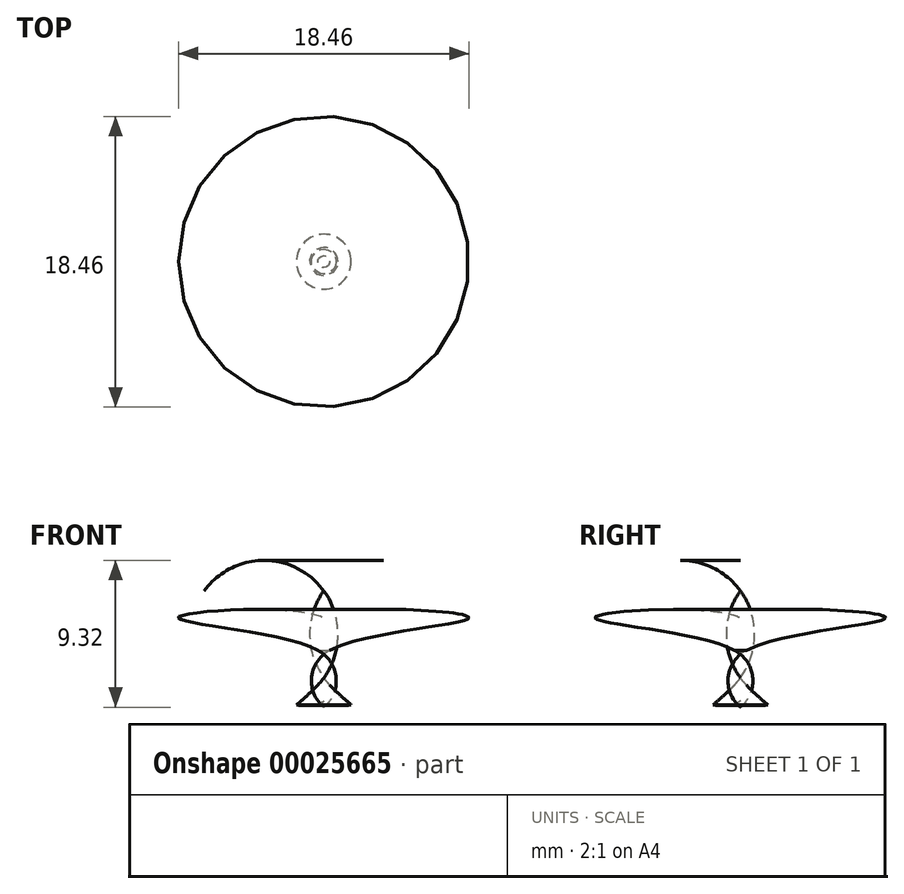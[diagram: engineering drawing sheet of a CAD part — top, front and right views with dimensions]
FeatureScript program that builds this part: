
annotation { "Feature Type Name" : "Feature", "Feature Type Description" : "" }
export const myFeature = defineFeature(function(context is Context, id is Id, definition is map)
    precondition{}
    {
        {
            var Q0;
            Q0=qCreatedBy(makeId("Front.planeOp"),FACE);
            var sketch = newSketch(context, id + "F0", { "sketchPlane" : qUnion([Q0])});
            skPoint(sketch, "E0.end.orphan", {"position": v(-15.16, 0) * mm});
            skPoint(sketch, "E1.end.orphan", {"position": v(0, 14.3) * mm});
            skPoint(sketch, "E1.start.orphan", {"position": v(0, 0) * mm});
            skPoint(sketch, "E2.endDerivative.orphan", {"position": v(-9.23, -2.95) * mm});
            skPoint(sketch, "E2.start.orphan", {"position": v(5.64, 0) * mm});
            skPoint(sketch, "E2.startDerivative.orphan", {"position": v(-9.23, 5.55) * mm});
            skFitSpline(sketch, "E3", {"points": [v(-1.74, 0) * mm, v(0, 3.22) * mm, v(-9.23, 5.55) * mm, v(0, 5.55) * mm, v(0, 4) * mm], "startDerivative": vector(19.84, 17.26) * mm, "endDerivative": vector(-7.42, -13.19) * mm});
            skLineSegment(sketch, "E4", {"start": v(0, 0) * mm, "end": v(0, 19.23) * mm});
            skFitSpline(sketch, "E5.trimOffspring", {"points": [v(-1.74, 0) * mm, v(0, 3.22) * mm, v(-9.23, 5.55) * mm, v(0, 5.55) * mm, v(0, 4) * mm], "startDerivative": vector(19.84, 17.26) * mm, "endDerivative": vector(-7.42, -13.19) * mm});
            skFitSpline(sketch, "E6", {"points": [v(-0.38, 1.19) * mm, v(-0.38, 3.48) * mm], "startDerivative": vector(0, 2.29) * mm, "endDerivative": vector(0, 2.29) * mm});
            skFitSpline(sketch, "E7", {"points": [v(-1.74, 0) * mm, v(-0.55, 0) * mm, v(0, 0.25) * mm], "startDerivative": vector(2.25, -0.18) * mm, "endDerivative": vector(1.18, 0.73) * mm});
            skSolve(sketch);
        }
        {
            var Q0;
            {var subQ3=sQuery(id+"F0.wireOp",EDGE,"E3");Q0=makeQuery(id+"F0.imprint","IMPRINT",FACE,{"disambiguationData":[TD([[makeQuery(id+"F0.imprint","IMPRINT",EDGE,{"derivedFrom":subQ3}),-1.0]])]});}
            var Q1;
            Q1=sQuery(id+"F0.wireOp",EDGE,"E4");
            revolve(context, id + "F1", {"entities" : qUnion([Q0]), "axis" : qUnion([Q1]), "revolveType" : RevolveType.FULL});
        }
    });
